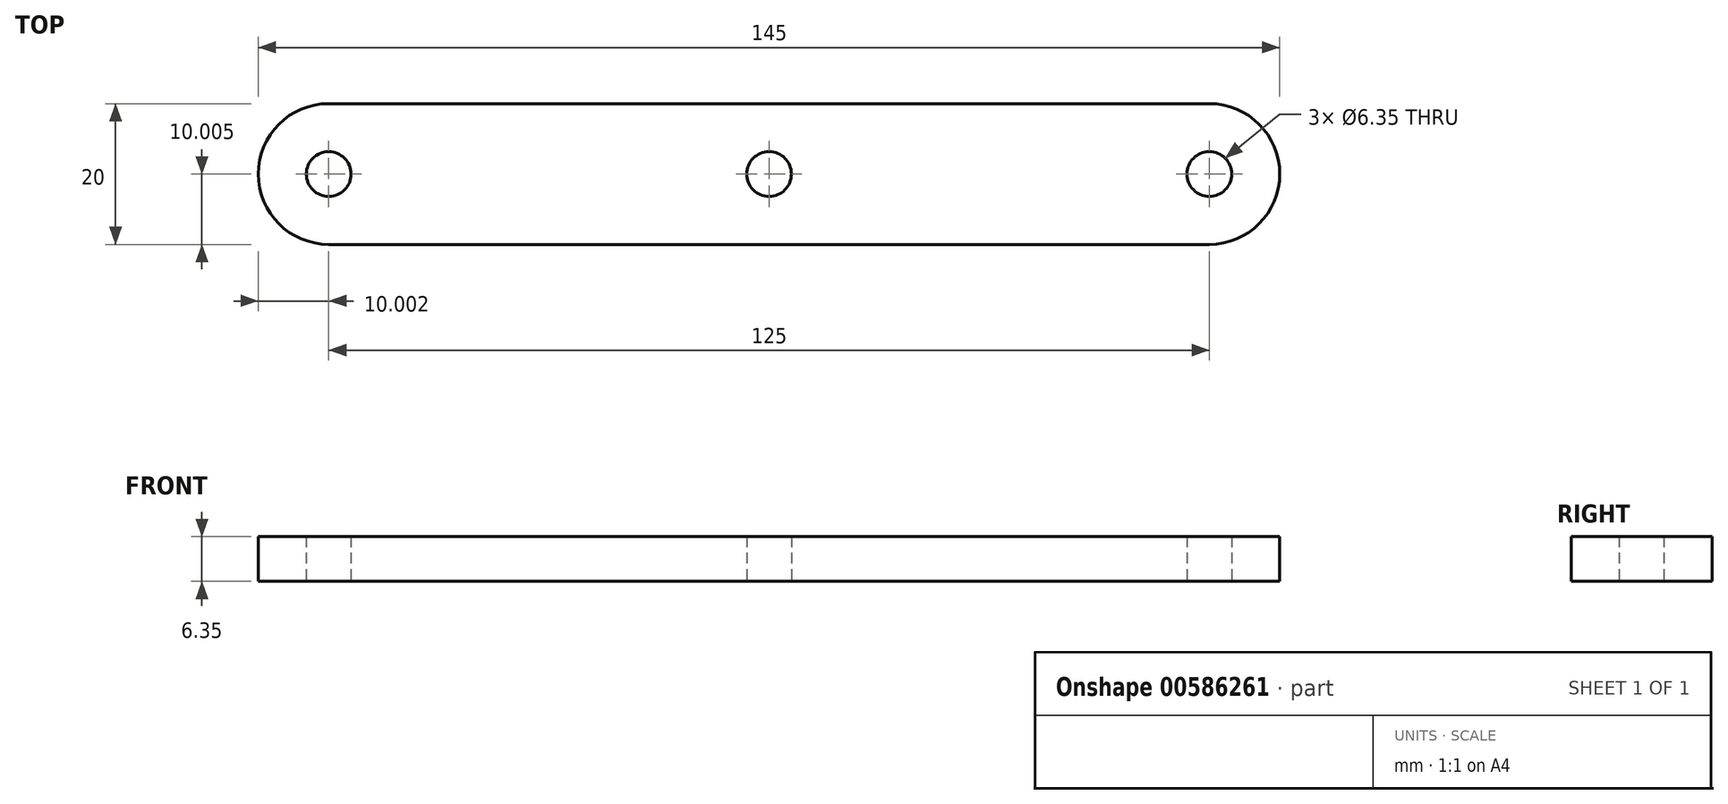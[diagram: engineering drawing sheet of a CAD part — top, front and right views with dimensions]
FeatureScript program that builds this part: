
annotation { "Feature Type Name" : "Feature", "Feature Type Description" : "" }
export const myFeature = defineFeature(function(context is Context, id is Id, definition is map)
    precondition{}
    {
        {
            var Q0;
            Q0=qCreatedBy(makeId("Top.planeOp"),FACE);
            var sketch = newSketch(context, id + "F0", { "sketchPlane" : qUnion([Q0])});
            skLineSegment(sketch, "E0", {"start": v(-50.57, -42.25) * mm, "end": v(74.43, -42.25) * mm});
            skLineSegment(sketch, "E1", {"start": v(-50.57, -62.25) * mm, "end": v(74.43, -62.25) * mm});
            skArc(sketch, "E2", {"start": v(-50.57, -42.25) * mm, "mid": v(-60.57, -52.25) * mm, "end": v(-50.57, -62.25) * mm});
            skArc(sketch, "E3", {"start": v(74.43, -62.25) * mm, "mid": v(84.43, -52.25) * mm, "end": v(74.43, -42.25) * mm});
            skSolve(sketch);
        }
        {
            var Q0;
            Q0=qCreatedBy(makeId("Top.planeOp"),FACE);
            var sketch = newSketch(context, id + "F1", { "sketchPlane" : qUnion([Q0])});
            skCircle(sketch, "E4", {"center": v(-50.57, -52.25) * mm, "radius": 3.18 * mm});
            skCircle(sketch, "E5", {"center": v(74.43, -52.25) * mm, "radius": 3.18 * mm});
            skCircle(sketch, "E6", {"center": v(11.93, -52.25) * mm, "radius": 3.18 * mm});
            skSolve(sketch);
        }
        {
            var Q0;
            Q0 = qSketchRegion(id + "F0", true);
            extrude(context, id + "F2", {"entities" : qUnion([Q0]), "depth" : 6.35 * mm, "offsetDistance" : 25 * mm});
        }
        {
            var Q0;
            Q0 = qSketchRegion(id + "F1", true);
            extrude(context, id + "F3", {"entities" : qUnion([Q0]), "operationType" : NewBodyOperationType.REMOVE, "endBound" : BoundingType.THROUGH_ALL, "depth" : 6.35 * mm, "offsetDistance" : 25 * mm});
        }
    });
